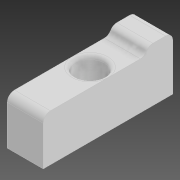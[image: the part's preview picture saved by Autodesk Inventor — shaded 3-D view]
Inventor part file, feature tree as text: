
AUTODESK INVENTOR PART (.ipt)
format: ipt  version: 2020 (Build 240168000, 168)  size: 128,000 bytes
history: native  units: in
note: dims shown in document units (in); Inventor stores cm internally (conversion verified against a paired STEP export)
features: extrude x4, sketch x2, fillet x2
ambient origin geometry x8: Origin, YZ Plane, XZ Plane, XY Plane, X Axis, Y Axis, Z Axis, Center Point
bodies: Solid1 (feature_tree)
feature tree (8):
  sketch  "Sketch1"  dims[d0=0.3937in d1=1.4173in]
  extrude  "Extrusion1"  Depth=1.4173in
  extrude  "Extrusion2"  Depth=0.5118in TaperAngle=0.0deg
  fillet  "Fillet1"  Radius=0.5906in
  sketch  "Sketch2"  dims[d2=0.2756in d3=0.5118in d4=0.0in d5=0.5906in d6=0.0in d7=0.0787in d8=0.315in d9=0.1575in d10=0.5906in d11=0.0in d12=0.3937in d13=0.0in d14=0.0394in]
  extrude  "Extrusion3"  Depth=0.0787in
  extrude  "Extrusion4"  Depth=0.0394in
  fillet  "Fillet2"  Radius=0.1575in
